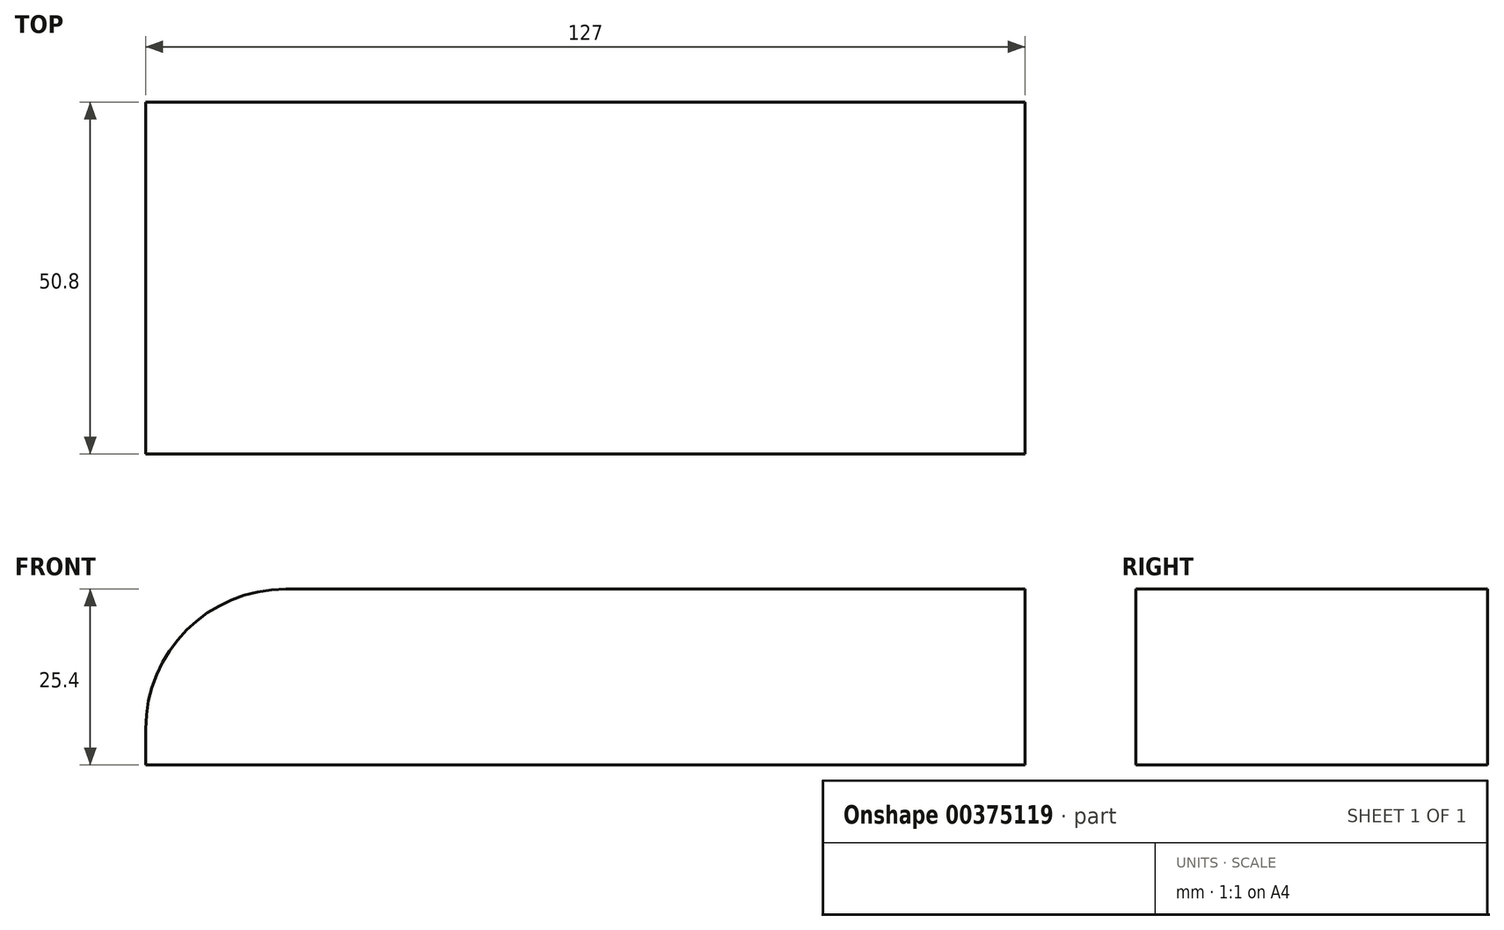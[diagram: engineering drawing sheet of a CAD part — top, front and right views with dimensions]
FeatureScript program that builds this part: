
annotation { "Feature Type Name" : "Feature", "Feature Type Description" : "" }
export const myFeature = defineFeature(function(context is Context, id is Id, definition is map)
    precondition{}
    {
        {
            var Q0;
            Q0=qCreatedBy(makeId("Top.planeOp"),FACE);
            var sketch = newSketch(context, id + "F0", { "sketchPlane" : qUnion([Q0])});
            skLineSegment(sketch, "E0.bottom", {"start": v(-63.5, -25.4) * mm, "end": v(63.5, -25.4) * mm});
            skLineSegment(sketch, "E0.top", {"start": v(-63.5, 25.4) * mm, "end": v(63.5, 25.4) * mm});
            skLineSegment(sketch, "E0.left", {"start": v(-63.5, -25.4) * mm, "end": v(-63.5, 25.4) * mm});
            skLineSegment(sketch, "E0.right", {"start": v(63.5, -25.4) * mm, "end": v(63.5, 25.4) * mm});
            skSolve(sketch);
        }
        {
            var Q0;
            Q0=makeQuery(id+"F0.imprint","IMPRINT",FACE,{"disambiguationData":[TD([[makeQuery(id+"F0.imprint","IMPRINT",EDGE,{"derivedFrom":sQuery(id+"F0.wireOp",EDGE,"E0.bottom")}),1.0]])]});
            extrude(context, id + "F1", {"entities" : qUnion([Q0]), "depth" : 25.4 * mm});
        }
        {
            var Q0;
            Q0=makeQuery(id+"F1.opExtrude","CAP_EDGE",EDGE,{"disambiguationData":[OSD([sQuery(id+"F0.wireOp",EDGE,"E0.left")])],"isStart":false});
            fillet(context, id + "F2", {"entities" : qUnion([Q0]), "radius" : 20.24 * mm, "tangentPropagation" : true, "allowEdgeOverflow" : false});
        }
    });
